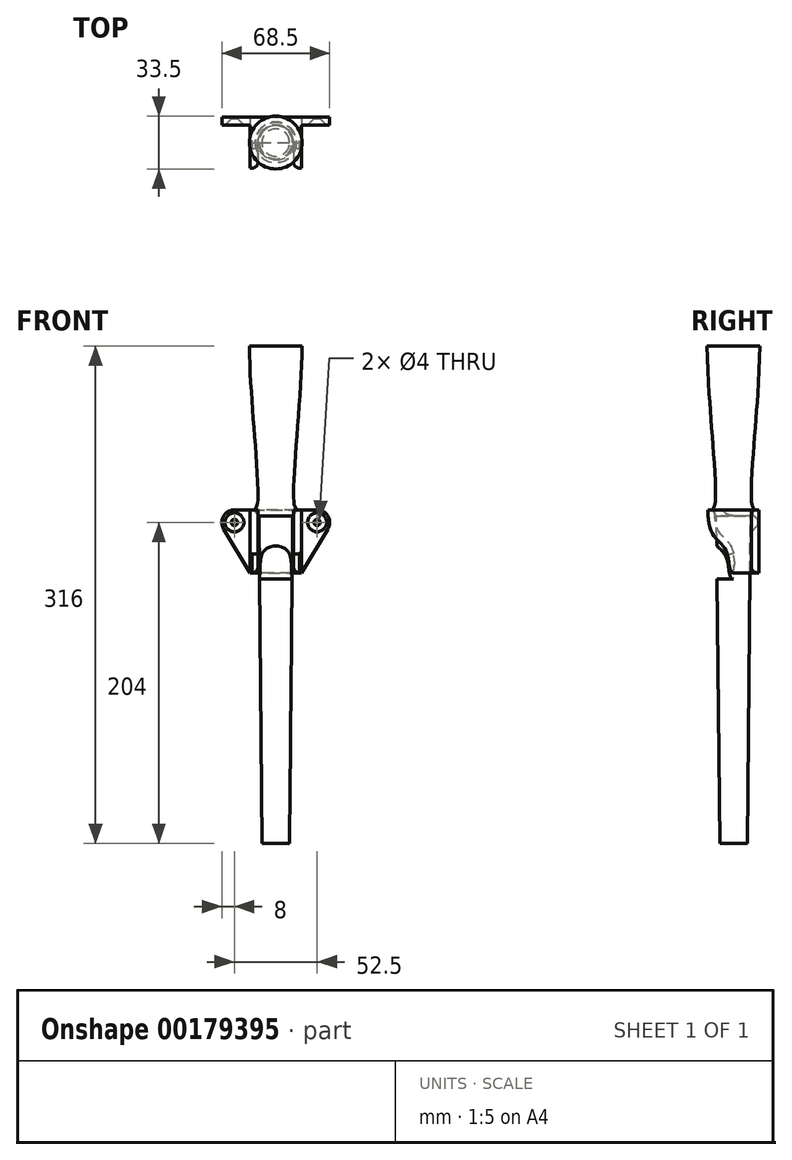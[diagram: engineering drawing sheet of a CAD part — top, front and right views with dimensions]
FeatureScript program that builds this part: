
annotation { "Feature Type Name" : "Feature", "Feature Type Description" : "" }
export const myFeature = defineFeature(function(context is Context, id is Id, definition is map)
    precondition{}
    {
        {
            assignVariable(context, id + "F0", {"name" : "Thickness", "anyValue" : 5});
        }
        {
            var Q0;
            Q0=qCreatedBy(makeId("Front.planeOp"),FACE);
            var sketch = newSketch(context, id + "F1", { "sketchPlane" : qUnion([Q0])});
            skLineSegment(sketch, "E0", {"start": v(-10.75, 0) * mm, "end": v(-8.75, -208) * mm});
            skLineSegment(sketch, "E1", {"start": v(-8.75, -208) * mm, "end": v(0, -208) * mm});
            skFitSpline(sketch, "E2", {"points": [v(-10.75, 0) * mm, v(-13, 4.5) * mm, v(-11.71, 7.49) * mm, v(-16.75, 108) * mm], "startDerivative": vector(-36.66, 38.6) * mm, "endDerivative": vector(-1.57, 152.15) * mm});
            skLineSegment(sketch, "E3", {"start": v(-16.75, 108) * mm, "end": v(0, 108) * mm});
            skLineSegment(sketch, "E4", {"start": v(0, 108) * mm, "end": v(0, -208) * mm});
            skSolve(sketch);
        }
        {
            var Q0;
            Q0=makeQuery(id+"F1.imprint","IMPRINT",FACE,{"disambiguationData":[TD([[makeQuery(id+"F1.imprint","IMPRINT",EDGE,{"derivedFrom":sQuery(id+"F1.wireOp",EDGE,"E0")}),1.0]])]});
            var Q1;
            Q1=sQuery(id+"F1.wireOp",EDGE,"E4");
            revolve(context, id + "F2", {"entities" : qUnion([Q0]), "axis" : qUnion([Q1]), "revolveType" : RevolveType.FULL});
        }
        {
            var Q0;
            Q0=qCreatedBy(makeId("Top.planeOp"),FACE);
            var sketch = newSketch(context, id + "F3", { "sketchPlane" : qUnion([Q0])});
            skArc(sketch, "E5.0", {"start": v(11.25, 0) * mm, "mid": v(0, 11.25) * mm, "end": v(-11.25, 0) * mm});
            skLineSegment(sketch, "E6", {"start": v(-11.25, 0) * mm, "end": v(-11.25, -16.25) * mm});
            skLineSegment(sketch, "E7", {"start": v(11.25, 0) * mm, "end": v(11.25, -16.25) * mm});
            skLineSegment(sketch, "E8.bottom", {"start": v(-16.25, 16.25) * mm, "end": v(16.25, 16.25) * mm});
            skLineSegment(sketch, "E8.top", {"start": v(-16.25, -16.25) * mm, "end": v(-11.25, -16.25) * mm});
            skLineSegment(sketch, "E8.left", {"start": v(-16.25, 16.25) * mm, "end": v(-16.25, -16.25) * mm});
            skLineSegment(sketch, "E8.right", {"start": v(16.25, 16.25) * mm, "end": v(16.25, -16.25) * mm});
            skLineSegment(sketch, "E9.trimOffspring", {"start": v(11.25, -16.25) * mm, "end": v(16.25, -16.25) * mm});
            skSolve(sketch);
        }
        {
            var Q0;
            {var subQ1=sQuery(id+"F3.wireOp",EDGE,"E6");Q0=makeQuery(id+"F3.imprint","IMPRINT",FACE,{"disambiguationData":[TD([[makeQuery(id+"F3.imprint","IMPRINT",EDGE,{"derivedFrom":subQ1}),-1.0]])]});}
            extrude(context, id + "F4", {"entities" : qUnion([Q0]), "oppositeDirection" : true, "depth" : 40 * mm});
        }
        {
            var Q0;
            Q0=makeQuery(id+"F4.opExtrude","SWEPT_FACE",FACE,{"disambiguationData":[OSD([sQuery(id+"F3.wireOp",EDGE,"E8.right")])]});
            var sketch = newSketch(context, id + "F5", { "sketchPlane" : qUnion([Q0])});
            skFitSpline(sketch, "E10", {"points": [v(-16.25, 0) * mm, v(-12.04, -17.17) * mm, v(-5.9, -23.78) * mm, v(-2.91, -33.4) * mm, v(0, -40) * mm], "startDerivative": vector(0, -79.33) * mm, "endDerivative": vector(33.31, 0) * mm});
            skLineSegment(sketch, "E11", {"start": v(-16.25, 0) * mm, "end": v(-16.25, -40) * mm});
            skLineSegment(sketch, "E12", {"start": v(-16.25, -40) * mm, "end": v(0, -40) * mm});
            skSolve(sketch);
        }
        {
            var Q0;
            Q0=makeQuery(id+"F5.imprint","IMPRINT",FACE,{"disambiguationData":[TD([[makeQuery(id+"F5.imprint","IMPRINT",EDGE,{"derivedFrom":sQuery(id+"F5.wireOp",EDGE,"E10")}),-1.0]])]});
            extrude(context, id + "F6", {"entities" : qUnion([Q0]), "operationType" : NewBodyOperationType.REMOVE, "endBound" : BoundingType.THROUGH_ALL, "oppositeDirection" : true, "depth" : 25 * mm});
        }
        {
            var Q0;
            Q0=makeQuery(id+"F4.opExtrude","SWEPT_FACE",FACE,{"disambiguationData":[OSD([sQuery(id+"F3.wireOp",EDGE,"E8.bottom")])]});
            var sketch = newSketch(context, id + "F7", { "sketchPlane" : qUnion([Q0])});
            skCircle(sketch, "E13", {"center": v(-26.25, -8) * mm, "radius": 2 * mm});
            skCircle(sketch, "E14.MirrorC", {"center": v(26.25, -8) * mm, "radius": 2 * mm});
            skLineSegment(sketch, "E15", {"start": v(-16.25, 0) * mm, "end": v(-16.25, -40) * mm});
            skLineSegment(sketch, "E16.MirrorCS", {"start": v(16.25, 0) * mm, "end": v(16.25, -40) * mm});
            skArc(sketch, "E17", {"start": v(-26.25, 0) * mm, "mid": v(-33.22, -4.07) * mm, "end": v(-33.1, -12.14) * mm});
            skArc(sketch, "E18.MirrorCS", {"start": v(26.25, 0) * mm, "mid": v(33.22, -4.07) * mm, "end": v(33.1, -12.14) * mm});
            skLineSegment(sketch, "E19", {"start": v(16.25, 0) * mm, "end": v(26.25, 0) * mm});
            skLineSegment(sketch, "E20", {"start": v(33.1, -12.14) * mm, "end": v(16.25, -40) * mm});
            skLineSegment(sketch, "E21.MirrorCS", {"start": v(-16.25, 0) * mm, "end": v(-26.25, 0) * mm});
            skLineSegment(sketch, "E22.MirrorCS", {"start": v(-33.1, -12.14) * mm, "end": v(-16.25, -40) * mm});
            skSolve(sketch);
        }
        {
            var Q0;
            Q0=qSketchRegion(id+"F7",true);
            extrude(context, id + "F8", {"entities" : qUnion([Q0]), "operationType" : NewBodyOperationType.ADD, "oppositeDirection" : true, "depth" : (getVariable(context, 'Thickness')) * mm});
        }
        {
            var Q0;
            Q0=makeQuery(id+"F8.opExtrude","CAP_EDGE",EDGE,{"disambiguationData":[OSD([sQuery(id+"F7.wireOp",EDGE,"E16.MirrorCS")])],"isStart":false});
            var Q1;
            Q1=makeQuery(id+"F8.opExtrude","CAP_EDGE",EDGE,{"disambiguationData":[OSD([sQuery(id+"F7.wireOp",EDGE,"E15")])],"isStart":false});
            var Q2;
            Q2=makeQuery(id+"F6.boolean.opBoolean","INTERSECT",EDGE,{"derivedFrom":[makeQuery(id+"F4.opExtrude","SWEPT_FACE",FACE,{"disambiguationData":[OSD([sQuery(id+"F3.wireOp",EDGE,"E6")])]}),makeQuery(id+"F6.opExtrude","SWEPT_FACE",FACE,{"disambiguationData":[OSD([sQuery(id+"F5.wireOp",EDGE,"E10")])]})]});
            var Q3;
            Q3=makeQuery(id+"F6.boolean.opBoolean","INTERSECT",EDGE,{"derivedFrom":[makeQuery(id+"F4.opExtrude","SWEPT_FACE",FACE,{"disambiguationData":[OSD([sQuery(id+"F3.wireOp",EDGE,"E7")])]}),makeQuery(id+"F6.opExtrude","SWEPT_FACE",FACE,{"disambiguationData":[OSD([sQuery(id+"F5.wireOp",EDGE,"E10")])]})]});
            fillet(context, id + "F9", {"entities" : qUnion([Q0, Q1, Q2, Q3]), "radius" : 4 * mm, "tangentPropagation" : true, "allowEdgeOverflow" : false});
        }
        {
            var Q0;
            Q0=makeQuery(id+"F8.opExtrude","CAP_EDGE",EDGE,{"disambiguationData":[OSD([sQuery(id+"F7.wireOp",EDGE,"E13")])],"isStart":false});
            var Q1;
            Q1=makeQuery(id+"F8.opExtrude","CAP_EDGE",EDGE,{"disambiguationData":[OSD([sQuery(id+"F7.wireOp",EDGE,"E14.MirrorC")])],"isStart":false});
            chamfer(context, id + "F10", {"entities" : qUnion([Q0, Q1]), "width" : 4 * mm, "tangentPropagation" : true});
        }
        {
            var Q0;
            Q0=makeQuery(id+"F2.opRevolve","SWEPT_BODY",BODY,{"disambiguationData":[OSD([sQuery(id+"F1.wireOp",EDGE,"E0"),sQuery(id+"F1.wireOp",EDGE,"E1"),sQuery(id+"F1.wireOp",EDGE,"E2"),sQuery(id+"F1.wireOp",EDGE,"E3"),sQuery(id+"F1.wireOp",EDGE,"E4")])]});
            transform(context, id + "F11", {"entities" : qUnion([Q0]), "transformType" : TransformType.TRANSLATION_3D, "dx" : 0 * mm, "dy" : 0 * mm, "dz" : -4 * mm, "makeCopy" : false});
        }
        {
            var Q0;
            Q0=makeQuery(id+"F2.opRevolve","SWEPT_BODY",BODY,{"disambiguationData":[OSD([sQuery(id+"F1.wireOp",EDGE,"E0"),sQuery(id+"F1.wireOp",EDGE,"E1"),sQuery(id+"F1.wireOp",EDGE,"E2"),sQuery(id+"F1.wireOp",EDGE,"E3"),sQuery(id+"F1.wireOp",EDGE,"E4")])]});
            var Q1;
            Q1=makeQuery(id+"F4.opExtrude","SWEPT_BODY",BODY,{"disambiguationData":[OSD([sQuery(id+"F3.wireOp",EDGE,"E5.0"),sQuery(id+"F3.wireOp",EDGE,"E6"),sQuery(id+"F3.wireOp",EDGE,"E7"),sQuery(id+"F3.wireOp",EDGE,"E8.bottom"),sQuery(id+"F3.wireOp",EDGE,"E8.top"),sQuery(id+"F3.wireOp",EDGE,"E8.left"),sQuery(id+"F3.wireOp",EDGE,"E8.right"),sQuery(id+"F3.wireOp",EDGE,"E9.trimOffspring")])]});
            booleanBodies(context, id + "F12", {"operationType" : BooleanOperationType.SUBTRACTION, "tools" : qUnion([Q0]), "targets" : qUnion([Q1]), "keepTools" : true});
        }
    });
